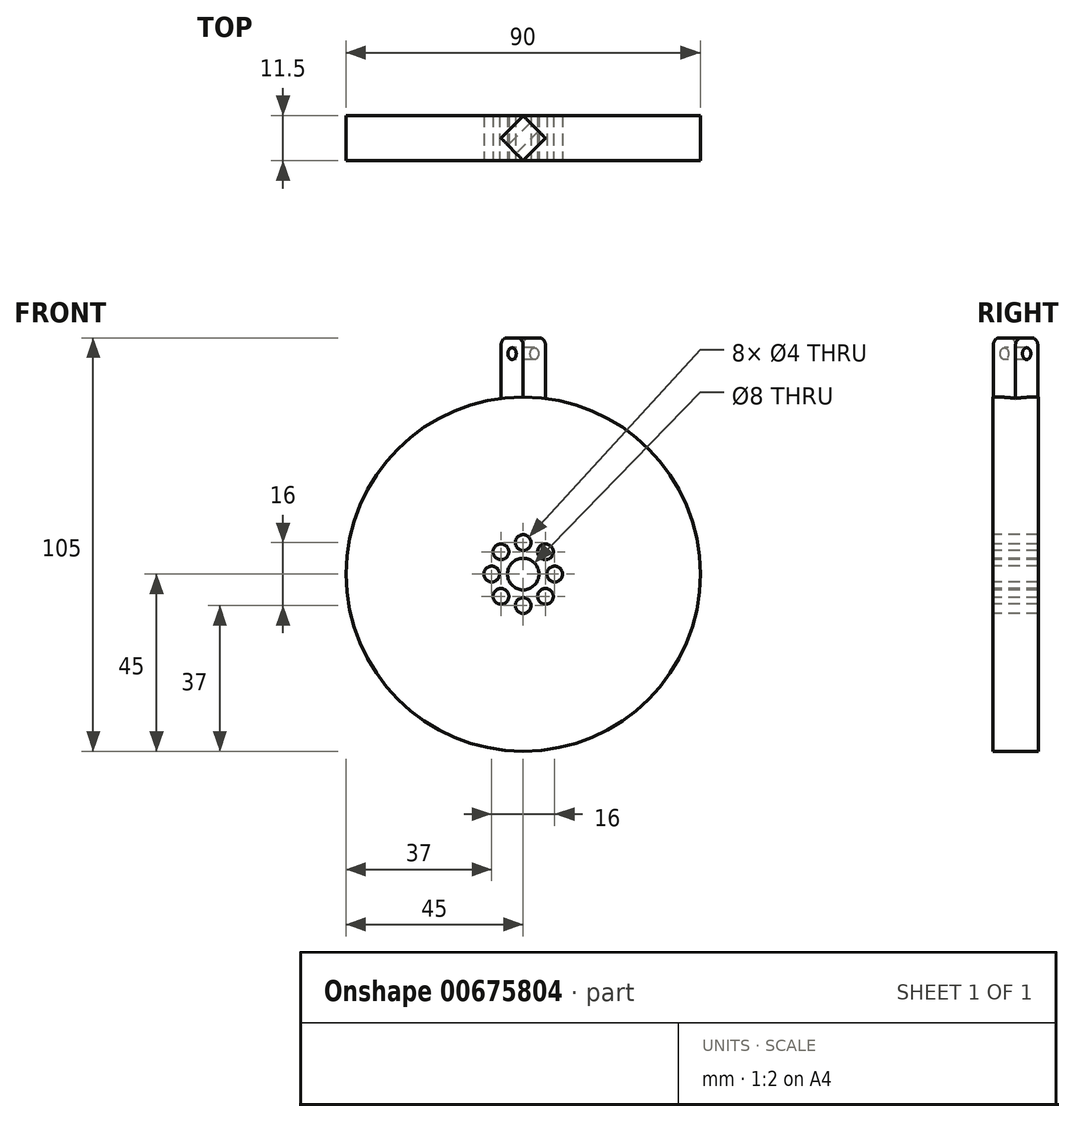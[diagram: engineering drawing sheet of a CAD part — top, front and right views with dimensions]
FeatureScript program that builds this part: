
annotation { "Feature Type Name" : "Feature", "Feature Type Description" : "" }
export const myFeature = defineFeature(function(context is Context, id is Id, definition is map)
    precondition{}
    {
        {
            var Q0;
            Q0=qCreatedBy(makeId("Top.planeOp"),FACE);
            var sketch = newSketch(context, id + "F0", { "sketchPlane" : qUnion([Q0])});
            skCircle(sketch, "E0", {"center": v(0, 0) * mm, "radius": 60 * mm});
            skLineSegment(sketch, "E1", {"start": v(0, 0) * mm, "end": v(0, 6) * mm});
            skLineSegment(sketch, "E2", {"start": v(0, 6) * mm, "end": v(0, -6) * mm});
            skSolve(sketch);
        }
        {
            var Q0;
            Q0=sQuery(id+"F0.wireOp",EDGE,"E0");
            cPlane(context, id + "F1", {"entities" : qUnion([Q0]), "cplaneType" : CPlaneType.LINE_ANGLE, "offset" : 25 * mm, "angle" : 45 * degree, "width" : 150 * mm, "height" : 150 * mm});
        }
        {
            var Q0;
            Q0=qCreatedBy(id+"F1.planeOp",FACE);
            var sketch = newSketch(context, id + "F2", { "sketchPlane" : qUnion([Q0])});
            skLineSegment(sketch, "E3", {"start": v(0, 0) * mm, "end": v(0, 60) * mm});
            skLineSegment(sketch, "E4.bottom", {"start": v(4, 0) * mm, "end": v(-4, 0) * mm});
            skLineSegment(sketch, "E4.top", {"start": v(4, 60) * mm, "end": v(-4, 60) * mm});
            skLineSegment(sketch, "E4.left", {"start": v(4, 0) * mm, "end": v(4, 60) * mm});
            skLineSegment(sketch, "E4.right", {"start": v(-4, 0) * mm, "end": v(-4, 60) * mm});
            skPoint(sketch, "E4.middle", {"position": v(0, 30) * mm});
            skSolve(sketch);
        }
        {
            var Q0;
            Q0 = qSketchRegion(id + "F2", true);
            extrude(context, id + "F3", {"entities" : qUnion([Q0]), "endBound" : BoundingType.SYMMETRIC, "oppositeDirection" : true, "depth" : 8 * mm, "offsetDistance" : 25 * mm});
        }
        {
            var Q0;
            Q0=qCreatedBy(makeId("Front.planeOp"),FACE);
            var sketch = newSketch(context, id + "F4", { "sketchPlane" : qUnion([Q0])});
            skCircle(sketch, "E5", {"center": v(0, 0) * mm, "radius": 45 * mm});
            skSolve(sketch);
        }
        {
            var Q0;
            Q0 = qSketchRegion(id + "F4", true);
            extrude(context, id + "F5", {"entities" : qUnion([Q0]), "operationType" : NewBodyOperationType.ADD, "endBound" : BoundingType.SYMMETRIC, "oppositeDirection" : true, "depth" : 11.5 * mm, "offsetDistance" : 25 * mm});
        }
        {
            var Q0;
            Q0=makeQuery(id+"F3.opExtrude","CAP_FACE",FACE,{"disambiguationData":[OSD([sQuery(id+"F2.wireOp",EDGE,"E4.bottom"),sQuery(id+"F2.wireOp",EDGE,"E4.top"),sQuery(id+"F2.wireOp",EDGE,"E4.left"),sQuery(id+"F2.wireOp",EDGE,"E4.right")])],"isStart":false});
            var sketch = newSketch(context, id + "F6", { "sketchPlane" : qUnion([Q0])});
            skLineSegment(sketch, "E6", {"start": v(0, 60) * mm, "end": v(0, 56) * mm});
            skCircle(sketch, "E7", {"center": v(0, 56) * mm, "radius": 1.5 * mm});
            skSolve(sketch);
        }
        {
            var Q0;
            Q0=makeQuery(id+"F6.imprint","IMPRINT",FACE,{"disambiguationData":[TD([[makeQuery(id+"F6.imprint","IMPRINT",EDGE,{"derivedFrom":sQuery(id+"F6.wireOp",EDGE,"E7")}),1.0]])]});
            extrude(context, id + "F7", {"entities" : qUnion([Q0]), "operationType" : NewBodyOperationType.REMOVE, "oppositeDirection" : true, "depth" : 25 * mm, "offsetDistance" : 25 * mm});
        }
        {
            var Q0;
            Q0=makeQuery(id+"FR7B6lL2js9cR43_1.3.F3.opExtrude","SWEPT_EDGE",EDGE,{"disambiguationData":[OSD([sQuery(id+"F2.wireOp",EDGE,"E4.top"),sQuery(id+"F2.wireOp",EDGE,"E4.right")])]});
            var Q1;
            Q1=makeQuery(id+"FR7B6lL2js9cR43_1.3.F3.opExtrude","SWEPT_EDGE",EDGE,{"disambiguationData":[OSD([sQuery(id+"F2.wireOp",EDGE,"E4.top"),sQuery(id+"F2.wireOp",EDGE,"E4.left")])]});
            var Q2;
            Q2=makeQuery(id+"FR7B6lL2js9cR43_1.2.F3.opExtrude","SWEPT_EDGE",EDGE,{"disambiguationData":[OSD([sQuery(id+"F2.wireOp",EDGE,"E4.top"),sQuery(id+"F2.wireOp",EDGE,"E4.right")])]});
            var Q3;
            Q3=makeQuery(id+"FR7B6lL2js9cR43_1.2.F3.opExtrude","SWEPT_EDGE",EDGE,{"disambiguationData":[OSD([sQuery(id+"F2.wireOp",EDGE,"E4.top"),sQuery(id+"F2.wireOp",EDGE,"E4.left")])]});
            var Q4;
            Q4=makeQuery(id+"FR7B6lL2js9cR43_1.1.F3.opExtrude","SWEPT_EDGE",EDGE,{"disambiguationData":[OSD([sQuery(id+"F2.wireOp",EDGE,"E4.top"),sQuery(id+"F2.wireOp",EDGE,"E4.right")])]});
            var Q5;
            Q5=makeQuery(id+"FR7B6lL2js9cR43_1.1.F3.opExtrude","SWEPT_EDGE",EDGE,{"disambiguationData":[OSD([sQuery(id+"F2.wireOp",EDGE,"E4.top"),sQuery(id+"F2.wireOp",EDGE,"E4.left")])]});
            var Q6;
            Q6=makeQuery(id+"F3.opExtrude","SWEPT_EDGE",EDGE,{"disambiguationData":[OSD([sQuery(id+"F2.wireOp",EDGE,"E4.top"),sQuery(id+"F2.wireOp",EDGE,"E4.right")])]});
            var Q7;
            Q7=makeQuery(id+"F3.opExtrude","SWEPT_EDGE",EDGE,{"disambiguationData":[OSD([sQuery(id+"F2.wireOp",EDGE,"E4.top"),sQuery(id+"F2.wireOp",EDGE,"E4.left")])]});
            var Q8;
            Q8=makeQuery(id+"FR7B6lL2js9cR43_1.11.F3.opExtrude","SWEPT_EDGE",EDGE,{"disambiguationData":[OSD([sQuery(id+"F2.wireOp",EDGE,"E4.top"),sQuery(id+"F2.wireOp",EDGE,"E4.left")])]});
            var Q9;
            Q9=makeQuery(id+"FR7B6lL2js9cR43_1.11.F3.opExtrude","SWEPT_EDGE",EDGE,{"disambiguationData":[OSD([sQuery(id+"F2.wireOp",EDGE,"E4.top"),sQuery(id+"F2.wireOp",EDGE,"E4.right")])]});
            var Q10;
            Q10=makeQuery(id+"FR7B6lL2js9cR43_1.10.F3.opExtrude","SWEPT_EDGE",EDGE,{"disambiguationData":[OSD([sQuery(id+"F2.wireOp",EDGE,"E4.top"),sQuery(id+"F2.wireOp",EDGE,"E4.left")])]});
            var Q11;
            Q11=makeQuery(id+"FR7B6lL2js9cR43_1.9.F3.opExtrude","SWEPT_EDGE",EDGE,{"disambiguationData":[OSD([sQuery(id+"F2.wireOp",EDGE,"E4.top"),sQuery(id+"F2.wireOp",EDGE,"E4.left")])]});
            var Q12;
            Q12=makeQuery(id+"FR7B6lL2js9cR43_1.10.F3.opExtrude","SWEPT_EDGE",EDGE,{"disambiguationData":[OSD([sQuery(id+"F2.wireOp",EDGE,"E4.top"),sQuery(id+"F2.wireOp",EDGE,"E4.right")])]});
            var Q13;
            Q13=makeQuery(id+"FR7B6lL2js9cR43_1.9.F3.opExtrude","SWEPT_EDGE",EDGE,{"disambiguationData":[OSD([sQuery(id+"F2.wireOp",EDGE,"E4.top"),sQuery(id+"F2.wireOp",EDGE,"E4.right")])]});
            var Q14;
            Q14=makeQuery(id+"FR7B6lL2js9cR43_1.8.F3.opExtrude","SWEPT_EDGE",EDGE,{"disambiguationData":[OSD([sQuery(id+"F2.wireOp",EDGE,"E4.top"),sQuery(id+"F2.wireOp",EDGE,"E4.left")])]});
            var Q15;
            Q15=makeQuery(id+"FR7B6lL2js9cR43_1.8.F3.opExtrude","SWEPT_EDGE",EDGE,{"disambiguationData":[OSD([sQuery(id+"F2.wireOp",EDGE,"E4.top"),sQuery(id+"F2.wireOp",EDGE,"E4.right")])]});
            var Q16;
            Q16=makeQuery(id+"FR7B6lL2js9cR43_1.7.F3.opExtrude","SWEPT_EDGE",EDGE,{"disambiguationData":[OSD([sQuery(id+"F2.wireOp",EDGE,"E4.top"),sQuery(id+"F2.wireOp",EDGE,"E4.left")])]});
            var Q17;
            Q17=makeQuery(id+"FR7B6lL2js9cR43_1.7.F3.opExtrude","SWEPT_EDGE",EDGE,{"disambiguationData":[OSD([sQuery(id+"F2.wireOp",EDGE,"E4.top"),sQuery(id+"F2.wireOp",EDGE,"E4.right")])]});
            var Q18;
            Q18=makeQuery(id+"FR7B6lL2js9cR43_1.6.F3.opExtrude","SWEPT_EDGE",EDGE,{"disambiguationData":[OSD([sQuery(id+"F2.wireOp",EDGE,"E4.top"),sQuery(id+"F2.wireOp",EDGE,"E4.left")])]});
            var Q19;
            Q19=makeQuery(id+"FR7B6lL2js9cR43_1.6.F3.opExtrude","SWEPT_EDGE",EDGE,{"disambiguationData":[OSD([sQuery(id+"F2.wireOp",EDGE,"E4.top"),sQuery(id+"F2.wireOp",EDGE,"E4.right")])]});
            var Q20;
            Q20=makeQuery(id+"FR7B6lL2js9cR43_1.5.F3.opExtrude","SWEPT_EDGE",EDGE,{"disambiguationData":[OSD([sQuery(id+"F2.wireOp",EDGE,"E4.top"),sQuery(id+"F2.wireOp",EDGE,"E4.left")])]});
            var Q21;
            Q21=makeQuery(id+"FR7B6lL2js9cR43_1.5.F3.opExtrude","SWEPT_EDGE",EDGE,{"disambiguationData":[OSD([sQuery(id+"F2.wireOp",EDGE,"E4.top"),sQuery(id+"F2.wireOp",EDGE,"E4.right")])]});
            var Q22;
            Q22=makeQuery(id+"FR7B6lL2js9cR43_1.4.F3.opExtrude","SWEPT_EDGE",EDGE,{"disambiguationData":[OSD([sQuery(id+"F2.wireOp",EDGE,"E4.top"),sQuery(id+"F2.wireOp",EDGE,"E4.left")])]});
            var Q23;
            Q23=makeQuery(id+"FR7B6lL2js9cR43_1.4.F3.opExtrude","SWEPT_EDGE",EDGE,{"disambiguationData":[OSD([sQuery(id+"F2.wireOp",EDGE,"E4.top"),sQuery(id+"F2.wireOp",EDGE,"E4.right")])]});
            fillet(context, id + "F8", {"entities" : qUnion([Q0, Q1, Q2, Q3, Q4, Q5, Q6, Q7, Q8, Q9, Q10, Q11, Q12, Q13, Q14, Q15, Q16, Q17, Q18, Q19, Q20, Q21, Q22, Q23]), "radius" : 2 * mm, "tangentPropagation" : true, "allowEdgeOverflow" : false});
        }
        {
            var Q0;
            Q0=makeQuery(id+"F5.opExtrude","CAP_FACE",FACE,{"disambiguationData":[OSD([sQuery(id+"F4.wireOp",EDGE,"E5")])],"isStart":true});
            var sketch = newSketch(context, id + "F9", { "sketchPlane" : qUnion([Q0])});
            skCircle(sketch, "E8", {"center": v(0, 0) * mm, "radius": 4 * mm});
            skLineSegment(sketch, "E9", {"start": v(0, 0) * mm, "end": v(0, 8) * mm});
            skCircle(sketch, "E10", {"center": v(0, 8) * mm, "radius": 2 * mm});
            skCircle(sketch, "E11.1.0", {"center": v(-5.66, 5.66) * mm, "radius": 2 * mm});
            skCircle(sketch, "E11.2.0", {"center": v(-8, 0) * mm, "radius": 2 * mm});
            skCircle(sketch, "E11.3.0", {"center": v(-5.66, -5.66) * mm, "radius": 2 * mm});
            skCircle(sketch, "E11.4.0", {"center": v(0, -8) * mm, "radius": 2 * mm});
            skCircle(sketch, "E11.5.0", {"center": v(5.66, -5.66) * mm, "radius": 2 * mm});
            skCircle(sketch, "E11.6.0", {"center": v(8, 0) * mm, "radius": 2 * mm});
            skCircle(sketch, "E11.7.0", {"center": v(5.66, 5.66) * mm, "radius": 2 * mm});
            skSolve(sketch);
        }
        {
            var Q0;
            Q0 = qSketchRegion(id + "F9", true);
            extrude(context, id + "F10", {"entities" : qUnion([Q0]), "operationType" : NewBodyOperationType.REMOVE, "oppositeDirection" : true, "depth" : 25 * mm, "offsetDistance" : 25 * mm});
        }
    });
